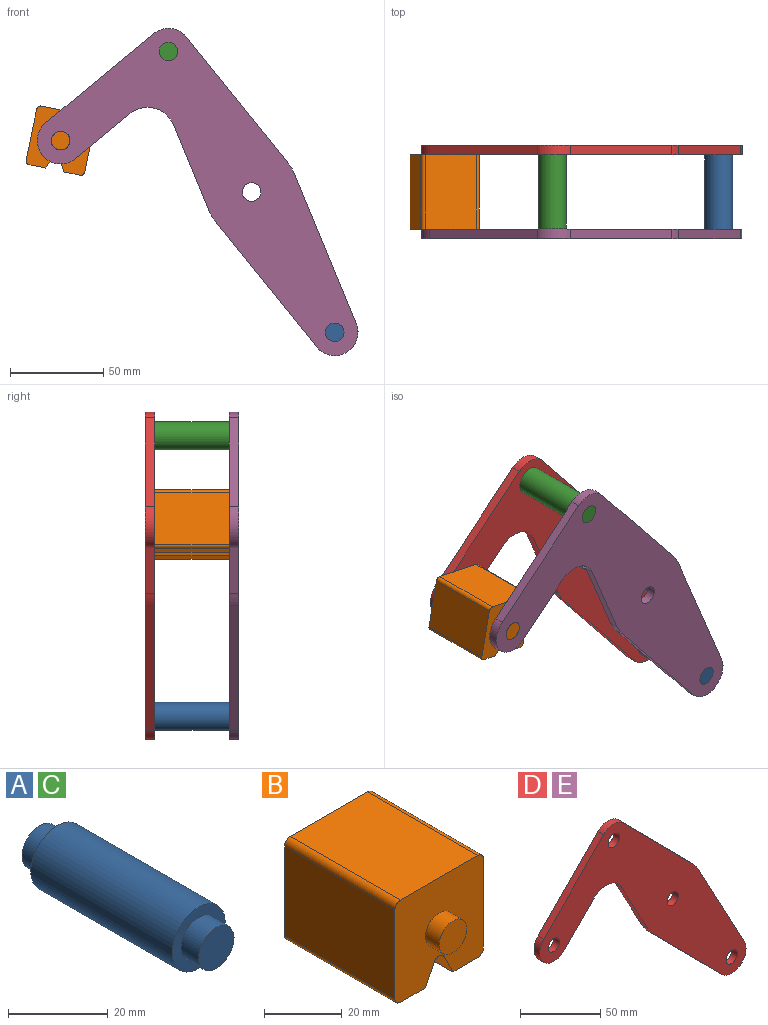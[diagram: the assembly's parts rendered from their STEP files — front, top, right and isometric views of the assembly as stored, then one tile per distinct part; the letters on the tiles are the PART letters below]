
ASSEMBLY  parts=5 mates=3
PART A: 7 faces, bbox 15x50x15 mm
  f0: cylinder r=7.5mm len=40mm, axis (0,-1,0), area 1885mm2, adj f2,f5
  f1: cylinder r=5mm len=10mm, axis (0,1,0), area 157.1mm2, adj f2,f3
  f2: plane 15x15mm, normal (0,-1,0), area 98.2mm2, adj f0,f1
  f3: plane 10x10mm, normal (0,-1,0), area 78.5mm2, adj f1
  f4: cylinder r=5mm len=10mm, axis (0,-1,0), area 157.1mm2, adj f5,f6
  f5: plane 15x15mm, normal (0,1,0), area 98.2mm2, adj f0,f4
  f6: plane 10x10mm, normal (0,1,0), area 78.5mm2, adj f4
PART B: 18 faces, bbox 32.1x50x32.1 mm
  f0: plane 40x28.08mm, normal (1,0,0), area 1123.1mm2, adj f4,f10,f13,f14
  f1: plane 40x9.04mm, normal (0,0,-1), area 361.6mm2, adj f2,f4,f10,f14
  f2: plane 40x6.42mm, normal (-0.89,0,-0.45), area 287.2mm2, adj f1,f4,f10,f15
  f3: plane 40x6.42mm, normal (0.89,0,-0.45), area 287.2mm2, adj f4,f5,f10,f15
  f4: plane 32.08x32.08mm, normal (0,-1,0), area 900.6mm2, adj f0,f1,f2,f3,f5,f6,f7,f9
  f5: plane 40x9.04mm, normal (0,0,-1), area 361.6mm2, adj f3,f4,f10,f16
  f6: plane 40x28.08mm, normal (0,0,1), area 1123.1mm2, adj f4,f10,f13,f17
  f7: plane 40x28.08mm, normal (-1,0,0), area 1123.1mm2, adj f4,f10,f16,f17
  f8: plane 10x10mm, normal (0,-1,0), area 78.5mm2, adj f9
  f9: cylinder r=5mm len=10mm, axis (0,1,0), area 157.1mm2, adj f4,f8
  f10: plane 32.08x32.08mm, normal (0,1,0), area 900.6mm2, adj f0,f1,f2,f3,f5,f6,f7,f12
  f11: plane 10x10mm, normal (0,1,0), area 78.5mm2, adj f12
  f12: cylinder r=5mm len=10mm, axis (0,-1,0), area 157.1mm2, adj f10,f11
  f13: cylinder r=2mm len=40mm, axis (0,1,0), area 125.7mm2, adj f0,f4,f6,f10
  f14: cylinder r=2mm len=40mm, axis (0,-1,0), area 125.7mm2, adj f0,f1,f4,f10
  f15: cylinder r=2mm len=40mm, axis (0,1,0), area 177.1mm2, adj f2,f3,f4,f10
  f16: cylinder r=2mm len=40mm, axis (0,1,0), area 125.7mm2, adj f4,f5,f7,f10
  f17: cylinder r=2mm len=40mm, axis (0,-1,0), area 125.7mm2, adj f4,f6,f7,f10
PART C: same geometry as A
PART D: 18 faces, bbox 181.7x5x165.8 mm
  f0: plane 43.49x23.35mm, normal (-0.88,0,-0.47), area 246.8mm2, adj f1,f14,f16,f17
  f1: cylinder r=25mm len=5.75mm, axis (0,1,0), area 35.8mm2, adj f0,f2,f16,f17
  f2: plane 61.6x60.87mm, normal (-0.71,0,-0.7), area 433mm2, adj f1,f3,f16,f17
  f3: cylinder r=12.5mm len=21.39mm, axis (0,1,0), area 178.4mm2, adj f2,f4,f16,f17
  f4: plane 76.3x40.96mm, normal (0.88,0,0.47), area 433mm2, adj f3,f5,f16,f17
  f5: cylinder r=25mm len=5.75mm, axis (0,1,0), area 35.8mm2, adj f4,f6,f16,f17
  f6: plane 61.6x60.87mm, normal (0.71,0,0.7), area 433mm2, adj f5,f7,f16,f17
  f7: cylinder r=12.5mm len=17.78mm, axis (0,1,0), area 98.9mm2, adj f6,f8,f16,f17
  f8: plane 53.35x52.71mm, normal (-0.71,0,0.7), area 375mm2, adj f7,f9,f16,f17
  f9: cylinder r=12.5mm len=21.39mm, axis (0,1,0), area 196.3mm2, adj f8,f10,f16,f17
  f10: plane 26.86x26.54mm, normal (0.71,0,-0.7), area 188.8mm2, adj f9,f14,f16,f17
  f11: cylinder r=5mm len=10mm, axis (0,1,0), area 157.1mm2, adj f16,f17
  f12: cylinder r=5mm len=10mm, axis (0,1,0), area 157.1mm2, adj f16,f17
  f13: cylinder r=5mm len=10mm, axis (0,1,0), area 157.1mm2, adj f16,f17
  f14: cylinder r=15mm len=23.89mm, axis (0,1,0), area 140.2mm2, adj f0,f10,f16,f17
  f15: cylinder r=5mm len=10mm, axis (0,1,0), area 157.1mm2, adj f16,f17
  f16: plane 181.66x165.78mm, normal (0,-1,0), area 8710.1mm2, adj f0,f1,f2,f3,f4,f5,f6,f7
  f17: plane 181.66x165.78mm, normal (0,1,0), area 8710.1mm2, adj f0,f1,f2,f3,f4,f5,f6,f7
PART E: same geometry as D
PLACE A rot(axis=(0,1,0),5.8deg) t=(89.19,-20,-150.57)mm
PLACE B rot(axis=(0,1,0),11.8deg) t=(-3.41,-20,-10.49)mm
PLACE C rot(axis=(0,1,0),5.8deg) t=(0,-20,0)mm
PLACE D rot(axis=(0,1,0),5.8deg) t=(0,25,0)mm
PLACE E rot(axis=(0,1,0),5.8deg) t=(0,-20,0)mm fixed
MATE revolute E.f9 <-> B.f9  axis (0,1,0) through (-102.43,-20,27.54)mm
MATE fastened C.f0 <-> D.f7  axis (0,1,0) through (-44.59,20,75.28)mm
MATE fastened A.f0 <-> E.f3  axis (0,-1,0) through (44.59,-20,-75.28)mm
